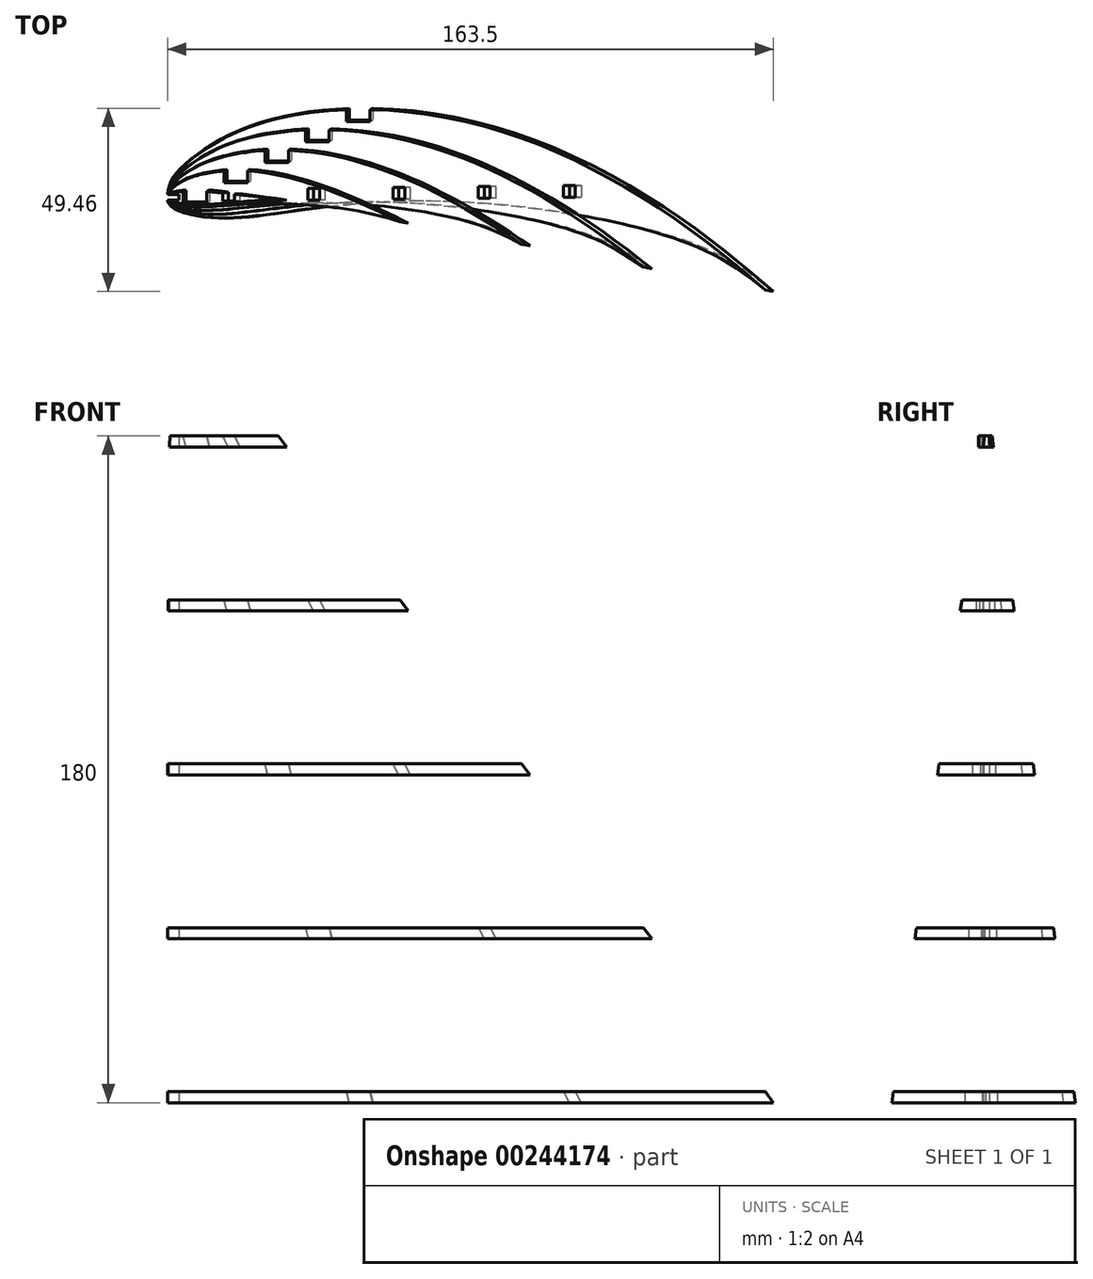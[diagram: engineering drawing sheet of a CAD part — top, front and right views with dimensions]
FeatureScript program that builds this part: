
annotation { "Feature Type Name" : "Feature", "Feature Type Description" : "" }
export const myFeature = defineFeature(function(context is Context, id is Id, definition is map)
    precondition{}
    {
        {
            var Q0;
            Q0=qCreatedBy(makeId("Top.planeOp"),FACE);
            var sketch = newSketch(context, id + "F0", { "sketchPlane" : qUnion([Q0])});
            skLineSegment(sketch, "E0", {"start": v(1.56, 5.68) * mm, "end": v(5.56, 9.57) * mm});
            skLineSegment(sketch, "E1", {"start": v(5.56, 9.57) * mm, "end": v(7.64, 11.4) * mm});
            skLineSegment(sketch, "E2", {"start": v(7.64, 11.4) * mm, "end": v(10.4, 13.54) * mm});
            skLineSegment(sketch, "E3", {"start": v(10.4, 13.54) * mm, "end": v(12.1, 14.65) * mm});
            skLineSegment(sketch, "E4", {"start": v(12.1, 14.65) * mm, "end": v(14.51, 16.01) * mm});
            skLineSegment(sketch, "E5", {"start": v(14.51, 16.01) * mm, "end": v(17.02, 17.22) * mm});
            skLineSegment(sketch, "E6", {"start": v(17.02, 17.22) * mm, "end": v(19.6, 18.28) * mm});
            skLineSegment(sketch, "E7", {"start": v(19.6, 18.28) * mm, "end": v(22.25, 19.22) * mm});
            skLineSegment(sketch, "E8", {"start": v(22.25, 19.22) * mm, "end": v(25.63, 20.25) * mm});
            skLineSegment(sketch, "E9", {"start": v(25.63, 20.25) * mm, "end": v(27.63, 20.8) * mm});
            skLineSegment(sketch, "E10", {"start": v(27.63, 20.8) * mm, "end": v(30.34, 21.45) * mm});
            skLineSegment(sketch, "E11", {"start": v(30.34, 21.45) * mm, "end": v(33.06, 22.02) * mm});
            skLineSegment(sketch, "E12", {"start": v(33.06, 22.02) * mm, "end": v(35.8, 22.52) * mm});
            skLineSegment(sketch, "E13", {"start": v(35.8, 22.52) * mm, "end": v(38.53, 22.94) * mm});
            skLineSegment(sketch, "E14", {"start": v(38.53, 22.94) * mm, "end": v(41.28, 23.3) * mm});
            skLineSegment(sketch, "E15", {"start": v(41.28, 23.3) * mm, "end": v(45.44, 23.69) * mm});
            skLineSegment(sketch, "E16", {"start": v(45.44, 23.69) * mm, "end": v(52.36, 24.01) * mm});
            skLineSegment(sketch, "E17", {"start": v(52.36, 24.01) * mm, "end": v(57.92, 23.98) * mm});
            skLineSegment(sketch, "E18", {"start": v(57.92, 23.98) * mm, "end": v(63.48, 23.67) * mm});
            skLineSegment(sketch, "E19", {"start": v(63.48, 23.67) * mm, "end": v(68.2, 23.2) * mm});
            skLineSegment(sketch, "E20", {"start": v(68.2, 23.2) * mm, "end": v(74.5, 22.25) * mm});
            skLineSegment(sketch, "E21", {"start": v(74.5, 22.25) * mm, "end": v(79.94, 21.16) * mm});
            skLineSegment(sketch, "E22", {"start": v(79.94, 21.16) * mm, "end": v(85.34, 19.84) * mm});
            skLineSegment(sketch, "E23", {"start": v(85.34, 19.84) * mm, "end": v(91.78, 17.96) * mm});
            skLineSegment(sketch, "E24", {"start": v(91.78, 17.96) * mm, "end": v(95.97, 16.57) * mm});
            skLineSegment(sketch, "E25", {"start": v(95.97, 16.57) * mm, "end": v(101.2, 14.66) * mm});
            skLineSegment(sketch, "E26", {"start": v(101.2, 14.66) * mm, "end": v(106.35, 12.57) * mm});
            skLineSegment(sketch, "E27", {"start": v(106.35, 12.57) * mm, "end": v(111.41, 10.3) * mm});
            skLineSegment(sketch, "E28", {"start": v(111.41, 10.3) * mm, "end": v(114.54, 8.79) * mm});
            skLineSegment(sketch, "E29", {"start": v(114.54, 8.79) * mm, "end": v(121.24, 5.25) * mm});
            skLineSegment(sketch, "E30", {"start": v(121.24, 5.25) * mm, "end": v(126.03, 2.48) * mm});
            skLineSegment(sketch, "E31", {"start": v(126.03, 2.48) * mm, "end": v(130.76, -0.45) * mm});
            skLineSegment(sketch, "E32", {"start": v(130.76, -0.45) * mm, "end": v(134.68, -3) * mm});
            skLineSegment(sketch, "E33", {"start": v(134.68, -3) * mm, "end": v(140.13, -6.74) * mm});
            skLineSegment(sketch, "E34", {"start": v(140.13, -6.74) * mm, "end": v(144.69, -10.02) * mm});
            skLineSegment(sketch, "E35", {"start": v(144.69, -10.02) * mm, "end": v(150.73, -14.63) * mm});
            skLineSegment(sketch, "E36", {"start": v(150.73, -14.63) * mm, "end": v(153.15, -16.57) * mm});
            skLineSegment(sketch, "E37", {"start": v(153.15, -16.57) * mm, "end": v(155.17, -18.23) * mm});
            skLineSegment(sketch, "E38", {"start": v(155.17, -18.23) * mm, "end": v(157.28, -19.98) * mm});
            skLineSegment(sketch, "E39", {"start": v(157.28, -19.98) * mm, "end": v(159.53, -21.87) * mm});
            skLineSegment(sketch, "E40", {"start": v(159.53, -21.87) * mm, "end": v(161.04, -23.14) * mm});
            skLineSegment(sketch, "E41", {"start": v(161.04, -23.14) * mm, "end": v(162.55, -24.41) * mm});
            skLineSegment(sketch, "E42", {"start": v(162.55, -24.41) * mm, "end": v(163.03, -24.83) * mm});
            skLineSegment(sketch, "E43", {"start": v(163.03, -24.83) * mm, "end": v(163.34, -25.1) * mm});
            skLineSegment(sketch, "E44", {"start": v(163.34, -25.1) * mm, "end": v(163.57, -25.34) * mm});
            skLineSegment(sketch, "E45", {"start": v(163.57, -25.34) * mm, "end": v(163.6, -25.41) * mm});
            skLineSegment(sketch, "E46", {"start": v(163.6, -25.41) * mm, "end": v(163.5, -25.38) * mm});
            skLineSegment(sketch, "E47", {"start": v(163.5, -25.38) * mm, "end": v(163.25, -25.24) * mm});
            skLineSegment(sketch, "E48", {"start": v(163.25, -25.24) * mm, "end": v(162.89, -25.02) * mm});
            skLineSegment(sketch, "E49", {"start": v(162.89, -25.02) * mm, "end": v(162.42, -24.7) * mm});
            skLineSegment(sketch, "E50", {"start": v(162.42, -24.7) * mm, "end": v(161.85, -24.33) * mm});
            skLineSegment(sketch, "E51", {"start": v(161.85, -24.33) * mm, "end": v(161.2, -23.89) * mm});
            skLineSegment(sketch, "E52", {"start": v(161.2, -23.89) * mm, "end": v(160.46, -23.39) * mm});
            skLineSegment(sketch, "E53", {"start": v(160.46, -23.39) * mm, "end": v(158.82, -22.27) * mm});
            skLineSegment(sketch, "E54", {"start": v(158.82, -22.27) * mm, "end": v(157.02, -21.04) * mm});
            skLineSegment(sketch, "E55", {"start": v(157.02, -21.04) * mm, "end": v(153.51, -18.72) * mm});
            skLineSegment(sketch, "E56", {"start": v(153.51, -18.72) * mm, "end": v(151.5, -17.45) * mm});
            skLineSegment(sketch, "E57", {"start": v(151.5, -17.45) * mm, "end": v(149.82, -16.42) * mm});
            skLineSegment(sketch, "E58", {"start": v(149.82, -16.42) * mm, "end": v(148.21, -15.5) * mm});
            skLineSegment(sketch, "E59", {"start": v(148.21, -15.5) * mm, "end": v(146.7, -14.65) * mm});
            skLineSegment(sketch, "E60", {"start": v(146.7, -14.65) * mm, "end": v(145.24, -13.9) * mm});
            skLineSegment(sketch, "E61", {"start": v(145.24, -13.9) * mm, "end": v(143.85, -13.2) * mm});
            skLineSegment(sketch, "E62", {"start": v(143.85, -13.2) * mm, "end": v(142.52, -12.6) * mm});
            skLineSegment(sketch, "E63", {"start": v(142.52, -12.6) * mm, "end": v(141.24, -12.04) * mm});
            skLineSegment(sketch, "E64", {"start": v(141.24, -12.04) * mm, "end": v(138.82, -11.11) * mm});
            skLineSegment(sketch, "E65", {"start": v(138.82, -11.11) * mm, "end": v(136.53, -10.36) * mm});
            skLineSegment(sketch, "E66", {"start": v(136.53, -10.36) * mm, "end": v(134.32, -9.76) * mm});
            skLineSegment(sketch, "E67", {"start": v(134.32, -9.76) * mm, "end": v(129.95, -8.78) * mm});
            skLineSegment(sketch, "E68", {"start": v(129.95, -8.78) * mm, "end": v(128.13, -8.4) * mm});
            skLineSegment(sketch, "E69", {"start": v(128.13, -8.4) * mm, "end": v(125.32, -7.82) * mm});
            skLineSegment(sketch, "E70", {"start": v(125.32, -7.82) * mm, "end": v(122.86, -7.3) * mm});
            skLineSegment(sketch, "E71", {"start": v(122.86, -7.3) * mm, "end": v(120.3, -6.74) * mm});
            skLineSegment(sketch, "E72", {"start": v(120.3, -6.74) * mm, "end": v(114.98, -5.62) * mm});
            skLineSegment(sketch, "E73", {"start": v(114.98, -5.62) * mm, "end": v(109.42, -4.5) * mm});
            skLineSegment(sketch, "E74", {"start": v(109.42, -4.5) * mm, "end": v(103.71, -3.46) * mm});
            skLineSegment(sketch, "E75", {"start": v(103.71, -3.46) * mm, "end": v(97.93, -2.53) * mm});
            skLineSegment(sketch, "E76", {"start": v(97.93, -2.53) * mm, "end": v(91.13, -1.7) * mm});
            skLineSegment(sketch, "E77", {"start": v(91.13, -1.7) * mm, "end": v(86.47, -1.3) * mm});
            skLineSegment(sketch, "E78", {"start": v(86.47, -1.3) * mm, "end": v(80.86, -1.04) * mm});
            skLineSegment(sketch, "E79", {"start": v(80.86, -1.04) * mm, "end": v(75.32, -0.97) * mm});
            skLineSegment(sketch, "E80", {"start": v(75.32, -0.97) * mm, "end": v(69.81, -1.08) * mm});
            skLineSegment(sketch, "E81", {"start": v(69.81, -1.08) * mm, "end": v(64.32, -1.32) * mm});
            skLineSegment(sketch, "E82", {"start": v(64.32, -1.32) * mm, "end": v(53.96, -2.02) * mm});
            skLineSegment(sketch, "E83", {"start": v(53.96, -2.02) * mm, "end": v(47.7, -2.53) * mm});
            skLineSegment(sketch, "E84", {"start": v(47.7, -2.53) * mm, "end": v(36.53, -3.57) * mm});
            skLineSegment(sketch, "E85", {"start": v(36.53, -3.57) * mm, "end": v(31.03, -4.15) * mm});
            skLineSegment(sketch, "E86", {"start": v(31.03, -4.15) * mm, "end": v(25.3, -4.8) * mm});
            skLineSegment(sketch, "E87", {"start": v(25.3, -4.8) * mm, "end": v(20.36, -5.36) * mm});
            skLineSegment(sketch, "E88", {"start": v(20.36, -5.36) * mm, "end": v(17.7, -5.56) * mm});
            skLineSegment(sketch, "E89", {"start": v(17.7, -5.56) * mm, "end": v(14.96, -5.63) * mm});
            skLineSegment(sketch, "E90", {"start": v(14.96, -5.63) * mm, "end": v(12.13, -5.52) * mm});
            skLineSegment(sketch, "E91", {"start": v(12.13, -5.52) * mm, "end": v(10.66, -5.39) * mm});
            skLineSegment(sketch, "E92", {"start": v(10.66, -5.39) * mm, "end": v(9.15, -5.2) * mm});
            skLineSegment(sketch, "E93", {"start": v(9.15, -5.2) * mm, "end": v(7.78, -4.97) * mm});
            skLineSegment(sketch, "E94", {"start": v(7.78, -4.97) * mm, "end": v(6.02, -4.6) * mm});
            skLineSegment(sketch, "E95", {"start": v(6.02, -4.6) * mm, "end": v(4.48, -4.16) * mm});
            skLineSegment(sketch, "E96", {"start": v(4.48, -4.16) * mm, "end": v(3.06, -3.62) * mm});
            skLineSegment(sketch, "E97", {"start": v(3.06, -3.62) * mm, "end": v(1.82, -2.95) * mm});
            skLineSegment(sketch, "E98", {"start": v(1.82, -2.95) * mm, "end": v(1.3, -2.56) * mm});
            skLineSegment(sketch, "E99", {"start": v(1.3, -2.56) * mm, "end": v(0.85, -2.13) * mm});
            skLineSegment(sketch, "E100", {"start": v(0.85, -2.13) * mm, "end": v(0.5, -1.66) * mm});
            skLineSegment(sketch, "E101", {"start": v(0.5, -1.66) * mm, "end": v(0.25, -1.2) * mm});
            skLineSegment(sketch, "E102", {"start": v(0.25, -1.2) * mm, "end": v(0.07, -0.6) * mm});
            skLineSegment(sketch, "E103", {"start": v(0.07, -0.6) * mm, "end": v(0, 0) * mm});
            skLineSegment(sketch, "E104", {"start": v(0, 0) * mm, "end": v(0.01, 0.63) * mm});
            skLineSegment(sketch, "E105", {"start": v(0.01, 0.63) * mm, "end": v(0.1, 1.3) * mm});
            skLineSegment(sketch, "E106", {"start": v(0.1, 1.3) * mm, "end": v(0.45, 2.7) * mm});
            skLineSegment(sketch, "E107", {"start": v(0.45, 2.7) * mm, "end": v(0.96, 4.17) * mm});
            skLineSegment(sketch, "E108", {"start": v(0.96, 4.17) * mm, "end": v(1.56, 5.68) * mm});
            skSolve(sketch);
        }
        {
            var Q0;
            Q0=qCreatedBy(makeId("Top.planeOp"),FACE);
            var sketch = newSketch(context, id + "F1", { "sketchPlane" : qUnion([Q0])});
            skPoint(sketch, "E109.0", {"position": v(0, 0) * mm});
            skPoint(sketch, "E109.1", {"position": v(5.56, 9.57) * mm});
            skPoint(sketch, "E109.2", {"position": v(22.25, 19.22) * mm});
            skPoint(sketch, "E109.3", {"position": v(57.92, 23.98) * mm});
            skPoint(sketch, "E109.4", {"position": v(101.2, 14.66) * mm});
            skPoint(sketch, "E109.5", {"position": v(140.13, -6.74) * mm});
            skPoint(sketch, "E109.6", {"position": v(163.6, -25.41) * mm});
            skPoint(sketch, "E109.7", {"position": v(0.25, -1.2) * mm});
            skPoint(sketch, "E109.8", {"position": v(1.82, -2.95) * mm});
            skPoint(sketch, "E109.9", {"position": v(12.13, -5.52) * mm});
            skPoint(sketch, "E109.10", {"position": v(0.96, 4.17) * mm});
            skPoint(sketch, "E109.11", {"position": v(31.03, -4.15) * mm});
            skPoint(sketch, "E109.12", {"position": v(75.32, -0.97) * mm});
            skPoint(sketch, "E109.13", {"position": v(142.52, -12.6) * mm});
            skFitSpline(sketch, "E110", {"points": [v(0, 0) * mm, v(0.96, 4.17) * mm, v(5.56, 9.57) * mm, v(22.25, 19.22) * mm, v(57.92, 23.98) * mm, v(101.2, 14.66) * mm, v(140.13, -6.74) * mm, v(163.6, -25.41) * mm], "startDerivative": vector(8.48, 68.87) * mm, "endDerivative": vector(134, -114.38) * mm});
            skFitSpline(sketch, "E111", {"points": [v(0, 0) * mm, v(0.25, -1.2) * mm, v(1.82, -2.95) * mm, v(12.13, -5.52) * mm, v(31.03, -4.15) * mm, v(75.32, -0.97) * mm, v(142.52, -12.6) * mm, v(163.6, -25.41) * mm], "startDerivative": vector(3.77, -32.14) * mm, "endDerivative": vector(102.14, -81.68) * mm});
            skSolve(sketch);
        }
        {
            var Q0;
            Q0=qCreatedBy(makeId("Top.planeOp"),FACE);
            cPlane(context, id + "F2", {"entities" : qUnion([Q0]), "cplaneType" : CPlaneType.OFFSET, "offset" : 180 * mm, "width" : 150 * mm, "height" : 150 * mm});
        }
        {
            var Q0;
            Q0=qCreatedBy(id+"F2.planeOp",FACE);
            var sketch = newSketch(context, id + "F3", { "sketchPlane" : qUnion([Q0])});
            skLineSegment(sketch, "E112", {"start": v(0, 0) * mm, "end": v(0.3, 0.38) * mm});
            skLineSegment(sketch, "E113", {"start": v(0.3, 0.38) * mm, "end": v(0.47, 0.56) * mm});
            skLineSegment(sketch, "E114", {"start": v(0.47, 0.56) * mm, "end": v(0.63, 0.72) * mm});
            skLineSegment(sketch, "E115", {"start": v(0.63, 0.72) * mm, "end": v(0.8, 0.86) * mm});
            skLineSegment(sketch, "E116", {"start": v(0.8, 0.86) * mm, "end": v(1, 1) * mm});
            skLineSegment(sketch, "E117", {"start": v(1, 1) * mm, "end": v(1.22, 1.1) * mm});
            skLineSegment(sketch, "E118", {"start": v(1.22, 1.1) * mm, "end": v(1.43, 1.2) * mm});
            skLineSegment(sketch, "E119", {"start": v(1.43, 1.2) * mm, "end": v(1.66, 1.26) * mm});
            skLineSegment(sketch, "E120", {"start": v(1.66, 1.26) * mm, "end": v(1.9, 1.32) * mm});
            skLineSegment(sketch, "E121", {"start": v(1.9, 1.32) * mm, "end": v(2.38, 1.4) * mm});
            skLineSegment(sketch, "E122", {"start": v(2.38, 1.4) * mm, "end": v(3.07, 1.49) * mm});
            skLineSegment(sketch, "E123", {"start": v(3.07, 1.49) * mm, "end": v(4.34, 1.61) * mm});
            skLineSegment(sketch, "E124", {"start": v(4.34, 1.61) * mm, "end": v(5.28, 1.69) * mm});
            skLineSegment(sketch, "E125", {"start": v(5.28, 1.69) * mm, "end": v(6.67, 1.76) * mm});
            skLineSegment(sketch, "E126", {"start": v(6.67, 1.76) * mm, "end": v(7.17, 1.76) * mm});
            skLineSegment(sketch, "E127", {"start": v(7.17, 1.76) * mm, "end": v(8.12, 1.75) * mm});
            skLineSegment(sketch, "E128", {"start": v(8.12, 1.75) * mm, "end": v(9.07, 1.72) * mm});
            skLineSegment(sketch, "E129", {"start": v(9.07, 1.72) * mm, "end": v(10.03, 1.66) * mm});
            skLineSegment(sketch, "E130", {"start": v(10.03, 1.66) * mm, "end": v(11.22, 1.58) * mm});
            skLineSegment(sketch, "E131", {"start": v(11.22, 1.58) * mm, "end": v(12.9, 1.43) * mm});
            skLineSegment(sketch, "E132", {"start": v(12.9, 1.43) * mm, "end": v(14.8, 1.24) * mm});
            skLineSegment(sketch, "E133", {"start": v(14.8, 1.24) * mm, "end": v(16.34, 1.07) * mm});
            skLineSegment(sketch, "E134", {"start": v(16.34, 1.07) * mm, "end": v(18.57, 0.8) * mm});
            skLineSegment(sketch, "E135", {"start": v(18.57, 0.8) * mm, "end": v(20.47, 0.56) * mm});
            skLineSegment(sketch, "E136", {"start": v(20.47, 0.56) * mm, "end": v(21.43, 0.45) * mm});
            skLineSegment(sketch, "E137", {"start": v(21.43, 0.45) * mm, "end": v(22.43, 0.33) * mm});
            skLineSegment(sketch, "E138", {"start": v(22.43, 0.33) * mm, "end": v(23.42, 0.21) * mm});
            skLineSegment(sketch, "E139", {"start": v(23.42, 0.21) * mm, "end": v(24.38, 0.1) * mm});
            skLineSegment(sketch, "E140", {"start": v(24.38, 0.1) * mm, "end": v(24.84, 0.04) * mm});
            skLineSegment(sketch, "E141", {"start": v(24.84, 0.04) * mm, "end": v(25.3, -0.01) * mm});
            skLineSegment(sketch, "E142", {"start": v(25.3, -0.01) * mm, "end": v(25.9, -0.09) * mm});
            skLineSegment(sketch, "E143", {"start": v(25.9, -0.09) * mm, "end": v(26.15, -0.12) * mm});
            skLineSegment(sketch, "E144", {"start": v(26.15, -0.12) * mm, "end": v(26.97, -0.22) * mm});
            skLineSegment(sketch, "E145", {"start": v(26.97, -0.22) * mm, "end": v(27.4, -0.27) * mm});
            skLineSegment(sketch, "E146", {"start": v(27.4, -0.27) * mm, "end": v(27.65, -0.29) * mm});
            skLineSegment(sketch, "E147", {"start": v(27.65, -0.29) * mm, "end": v(27.9, -0.3) * mm});
            skLineSegment(sketch, "E148", {"start": v(27.9, -0.3) * mm, "end": v(28.16, -0.32) * mm});
            skLineSegment(sketch, "E149", {"start": v(28.16, -0.32) * mm, "end": v(28.45, -0.34) * mm});
            skLineSegment(sketch, "E150", {"start": v(28.45, -0.34) * mm, "end": v(28.76, -0.35) * mm});
            skLineSegment(sketch, "E151", {"start": v(28.76, -0.35) * mm, "end": v(28.93, -0.36) * mm});
            skLineSegment(sketch, "E152", {"start": v(28.93, -0.36) * mm, "end": v(29.42, -0.37) * mm});
            skLineSegment(sketch, "E153", {"start": v(29.42, -0.37) * mm, "end": v(29.57, -0.37) * mm});
            skLineSegment(sketch, "E154", {"start": v(29.57, -0.37) * mm, "end": v(29.71, -0.38) * mm});
            skLineSegment(sketch, "E155", {"start": v(29.71, -0.38) * mm, "end": v(29.83, -0.38) * mm});
            skLineSegment(sketch, "E156", {"start": v(29.83, -0.38) * mm, "end": v(29.92, -0.38) * mm});
            skLineSegment(sketch, "E157", {"start": v(29.92, -0.38) * mm, "end": v(29.98, -0.38) * mm});
            skLineSegment(sketch, "E158", {"start": v(29.98, -0.38) * mm, "end": v(30, -0.39) * mm});
            skLineSegment(sketch, "E159", {"start": v(30, -0.39) * mm, "end": v(29.98, -0.39) * mm});
            skLineSegment(sketch, "E160", {"start": v(29.98, -0.39) * mm, "end": v(29.92, -0.4) * mm});
            skLineSegment(sketch, "E161", {"start": v(29.92, -0.4) * mm, "end": v(29.83, -0.4) * mm});
            skLineSegment(sketch, "E162", {"start": v(29.83, -0.4) * mm, "end": v(29.72, -0.4) * mm});
            skLineSegment(sketch, "E163", {"start": v(29.72, -0.4) * mm, "end": v(29.58, -0.4) * mm});
            skLineSegment(sketch, "E164", {"start": v(29.58, -0.4) * mm, "end": v(29.42, -0.4) * mm});
            skLineSegment(sketch, "E165", {"start": v(29.42, -0.4) * mm, "end": v(28.93, -0.42) * mm});
            skLineSegment(sketch, "E166", {"start": v(28.93, -0.42) * mm, "end": v(28.76, -0.42) * mm});
            skLineSegment(sketch, "E167", {"start": v(28.76, -0.42) * mm, "end": v(28.45, -0.43) * mm});
            skLineSegment(sketch, "E168", {"start": v(28.45, -0.43) * mm, "end": v(28.17, -0.44) * mm});
            skLineSegment(sketch, "E169", {"start": v(28.17, -0.44) * mm, "end": v(27.9, -0.46) * mm});
            skLineSegment(sketch, "E170", {"start": v(27.9, -0.46) * mm, "end": v(27.65, -0.47) * mm});
            skLineSegment(sketch, "E171", {"start": v(27.65, -0.47) * mm, "end": v(27.4, -0.49) * mm});
            skLineSegment(sketch, "E172", {"start": v(27.4, -0.49) * mm, "end": v(26.96, -0.52) * mm});
            skLineSegment(sketch, "E173", {"start": v(26.96, -0.52) * mm, "end": v(26.14, -0.6) * mm});
            skLineSegment(sketch, "E174", {"start": v(26.14, -0.6) * mm, "end": v(25.86, -0.62) * mm});
            skLineSegment(sketch, "E175", {"start": v(25.86, -0.62) * mm, "end": v(25.3, -0.68) * mm});
            skLineSegment(sketch, "E176", {"start": v(25.3, -0.68) * mm, "end": v(24.84, -0.72) * mm});
            skLineSegment(sketch, "E177", {"start": v(24.84, -0.72) * mm, "end": v(24.37, -0.77) * mm});
            skLineSegment(sketch, "E178", {"start": v(24.37, -0.77) * mm, "end": v(23.4, -0.86) * mm});
            skLineSegment(sketch, "E179", {"start": v(23.4, -0.86) * mm, "end": v(22.42, -0.95) * mm});
            skLineSegment(sketch, "E180", {"start": v(22.42, -0.95) * mm, "end": v(21.43, -1.04) * mm});
            skLineSegment(sketch, "E181", {"start": v(21.43, -1.04) * mm, "end": v(20.45, -1.13) * mm});
            skLineSegment(sketch, "E182", {"start": v(20.45, -1.13) * mm, "end": v(18.55, -1.3) * mm});
            skLineSegment(sketch, "E183", {"start": v(18.55, -1.3) * mm, "end": v(16.28, -1.52) * mm});
            skLineSegment(sketch, "E184", {"start": v(16.28, -1.52) * mm, "end": v(12.87, -1.8) * mm});
            skLineSegment(sketch, "E185", {"start": v(12.87, -1.8) * mm, "end": v(11.19, -1.9) * mm});
            skLineSegment(sketch, "E186", {"start": v(11.19, -1.9) * mm, "end": v(10, -1.95) * mm});
            skLineSegment(sketch, "E187", {"start": v(10, -1.95) * mm, "end": v(9.03, -1.98) * mm});
            skLineSegment(sketch, "E188", {"start": v(9.03, -1.98) * mm, "end": v(8.08, -1.98) * mm});
            skLineSegment(sketch, "E189", {"start": v(8.08, -1.98) * mm, "end": v(7.13, -1.96) * mm});
            skLineSegment(sketch, "E190", {"start": v(7.13, -1.96) * mm, "end": v(6.6, -1.93) * mm});
            skLineSegment(sketch, "E191", {"start": v(6.6, -1.93) * mm, "end": v(5.24, -1.83) * mm});
            skLineSegment(sketch, "E192", {"start": v(5.24, -1.83) * mm, "end": v(4.3, -1.74) * mm});
            skLineSegment(sketch, "E193", {"start": v(4.3, -1.74) * mm, "end": v(3.04, -1.58) * mm});
            skLineSegment(sketch, "E194", {"start": v(3.04, -1.58) * mm, "end": v(2.35, -1.47) * mm});
            skLineSegment(sketch, "E195", {"start": v(2.35, -1.47) * mm, "end": v(1.87, -1.37) * mm});
            skLineSegment(sketch, "E196", {"start": v(1.87, -1.37) * mm, "end": v(1.64, -1.3) * mm});
            skLineSegment(sketch, "E197", {"start": v(1.64, -1.3) * mm, "end": v(1.41, -1.22) * mm});
            skLineSegment(sketch, "E198", {"start": v(1.41, -1.22) * mm, "end": v(1.2, -1.13) * mm});
            skLineSegment(sketch, "E199", {"start": v(1.2, -1.13) * mm, "end": v(1, -1.01) * mm});
            skLineSegment(sketch, "E200", {"start": v(1, -1.01) * mm, "end": v(0.77, -0.86) * mm});
            skLineSegment(sketch, "E201", {"start": v(0.77, -0.86) * mm, "end": v(0.62, -0.73) * mm});
            skLineSegment(sketch, "E202", {"start": v(0.62, -0.73) * mm, "end": v(0.46, -0.57) * mm});
            skLineSegment(sketch, "E203", {"start": v(0.46, -0.57) * mm, "end": v(0.3, -0.38) * mm});
            skLineSegment(sketch, "E204", {"start": v(0.3, -0.38) * mm, "end": v(0, 0) * mm});
            skSolve(sketch);
        }
        {
            var Q0;
            Q0=qCreatedBy(id+"F2.planeOp",FACE);
            var sketch = newSketch(context, id + "F4", { "sketchPlane" : qUnion([Q0])});
            skPoint(sketch, "E205.0", {"position": v(0, 0) * mm});
            skPoint(sketch, "E205.1", {"position": v(0.47, 0.56) * mm});
            skPoint(sketch, "E205.2", {"position": v(1, 1) * mm});
            skPoint(sketch, "E205.3", {"position": v(1.9, 1.32) * mm});
            skPoint(sketch, "E205.4", {"position": v(6.67, 1.76) * mm});
            skPoint(sketch, "E205.5", {"position": v(10.03, 1.66) * mm});
            skPoint(sketch, "E205.6", {"position": v(18.57, 0.8) * mm});
            skPoint(sketch, "E205.7", {"position": v(30, -0.39) * mm});
            skPoint(sketch, "E205.8", {"position": v(0.46, -0.57) * mm});
            skPoint(sketch, "E205.9", {"position": v(1, -1.01) * mm});
            skPoint(sketch, "E205.10", {"position": v(1.87, -1.37) * mm});
            skPoint(sketch, "E205.11", {"position": v(6.6, -1.93) * mm});
            skPoint(sketch, "E205.12", {"position": v(10, -1.95) * mm});
            skPoint(sketch, "E205.13", {"position": v(18.55, -1.3) * mm});
            skFitSpline(sketch, "E206", {"points": [v(0, 0) * mm, v(0.47, 0.56) * mm, v(1, 1) * mm, v(1.9, 1.32) * mm, v(6.67, 1.76) * mm, v(10.03, 1.66) * mm, v(18.57, 0.8) * mm, v(30, -0.39) * mm], "startDerivative": vector(6.75, 8.84) * mm, "endDerivative": vector(44, -4.53) * mm});
            skFitSpline(sketch, "E207", {"points": [v(0, 0) * mm, v(0.46, -0.57) * mm, v(1, -1.01) * mm, v(1.87, -1.37) * mm, v(6.6, -1.93) * mm, v(10, -1.95) * mm, v(18.55, -1.3) * mm, v(30, -0.39) * mm], "startDerivative": vector(6.61, -8.92) * mm, "endDerivative": vector(44.1, 3.52) * mm});
            skSolve(sketch);
        }
        {
            var Q0;
            Q0=qCreatedBy(makeId("Front.planeOp"),FACE);
            var sketch = newSketch(context, id + "F5", { "sketchPlane" : qUnion([Q0])});
            skLineSegment(sketch, "E208", {"start": v(0, 0) * mm, "end": v(0, 180) * mm});
            skSolve(sketch);
        }
        {
            var Q0;
            Q0=makeQuery(id+"F1.imprint","IMPRINT",FACE,{"disambiguationData":[TD([[makeQuery(id+"F1.imprint","IMPRINT",EDGE,{"derivedFrom":sQuery(id+"F1.wireOp",EDGE,"E110")}),-1.0]])]});
            var Q1;
            Q1=makeQuery(id+"F4.imprint","IMPRINT",FACE,{"disambiguationData":[TD([[makeQuery(id+"F4.imprint","IMPRINT",EDGE,{"derivedFrom":sQuery(id+"F4.wireOp",EDGE,"E206")}),-1.0]])]});
            var Q2;
            Q2=sQuery(id+"F5.wireOp",EDGE,"E208");
            loft(context, id + "F6", {"addGuides" : true, "sheetProfilesArray" : [{ "sheetProfileEntities" : qUnion([Q0]) }, { "sheetProfileEntities" : qUnion([Q1]) }], "guidesArray" : [{ "guideEntities" : qUnion([Q2]), "guideDerivativeType" : LoftGuideDerivativeType.DEFAULT, "guideDerivativeMagnitude" : 1 }]});
        }
        {
            var Q0;
            Q0=qCreatedBy(makeId("Front.planeOp"),FACE);
            var sketch = newSketch(context, id + "F7", { "sketchPlane" : qUnion([Q0])});
            skLineSegment(sketch, "E209", {"start": v(0, 0) * mm, "end": v(0, 3) * mm, "construction": true});
            skLineSegment(sketch, "E210.bottom", {"start": v(0, 3) * mm, "end": v(200, 3) * mm});
            skLineSegment(sketch, "E210.top", {"start": v(0, 44.25) * mm, "end": v(200, 44.25) * mm});
            skLineSegment(sketch, "E210.left", {"start": v(0, 3) * mm, "end": v(0, 44.25) * mm});
            skLineSegment(sketch, "E210.right", {"start": v(200, 3) * mm, "end": v(200, 44.25) * mm});
            skLineSegment(sketch, "E211.0.1.0", {"start": v(200, 47.25) * mm, "end": v(200, 88.5) * mm});
            skLineSegment(sketch, "E211.0.1.1", {"start": v(0, 47.25) * mm, "end": v(0, 88.5) * mm});
            skLineSegment(sketch, "E211.0.1.2", {"start": v(0, 88.5) * mm, "end": v(200, 88.5) * mm});
            skLineSegment(sketch, "E211.0.1.3", {"start": v(0, 47.25) * mm, "end": v(200, 47.25) * mm});
            skLineSegment(sketch, "E211.0.1.4", {"start": v(0, 44.25) * mm, "end": v(0, 47.25) * mm, "construction": true});
            skLineSegment(sketch, "E211.0.2.0", {"start": v(200, 91.5) * mm, "end": v(200, 132.75) * mm});
            skLineSegment(sketch, "E211.0.2.1", {"start": v(0, 91.5) * mm, "end": v(0, 132.75) * mm});
            skLineSegment(sketch, "E211.0.2.2", {"start": v(0, 132.75) * mm, "end": v(200, 132.75) * mm});
            skLineSegment(sketch, "E211.0.2.3", {"start": v(0, 91.5) * mm, "end": v(200, 91.5) * mm});
            skLineSegment(sketch, "E211.0.2.4", {"start": v(0, 88.5) * mm, "end": v(0, 91.5) * mm, "construction": true});
            skLineSegment(sketch, "E211.0.3.0", {"start": v(200, 135.75) * mm, "end": v(200, 177) * mm});
            skLineSegment(sketch, "E211.0.3.1", {"start": v(0, 135.75) * mm, "end": v(0, 177) * mm});
            skLineSegment(sketch, "E211.0.3.2", {"start": v(0, 177) * mm, "end": v(200, 177) * mm});
            skLineSegment(sketch, "E211.0.3.3", {"start": v(0, 135.75) * mm, "end": v(200, 135.75) * mm});
            skLineSegment(sketch, "E211.0.3.4", {"start": v(0, 132.75) * mm, "end": v(0, 135.75) * mm, "construction": true});
            skLineSegment(sketch, "E211.direction1", {"start": v(0, 0) * mm, "end": v(25, 0) * mm, "construction": true});
            skLineSegment(sketch, "E211.direction2", {"start": v(0, 0) * mm, "end": v(0, 44.25) * mm, "construction": true});
            skSolve(sketch);
        }
        {
            var Q0;
            Q0 = qSketchRegion(id + "F7", true);
            extrude(context, id + "F8", {"entities" : qUnion([Q0]), "operationType" : NewBodyOperationType.REMOVE, "oppositeDirection" : true, "depth" : 100 * mm, "offsetDistance" : 25 * mm, "hasSecondDirection" : true, "secondDirectionOppositeDirection" : false, "secondDirectionDepth" : 100 * mm});
        }
        {
            var Q0;
            Q0=qCreatedBy(makeId("Top.planeOp"),FACE);
            var sketch = newSketch(context, id + "F9", { "sketchPlane" : qUnion([Q0])});
            skLineSegment(sketch, "E212", {"start": v(0, 0) * mm, "end": v(0, 0.8) * mm});
            skLineSegment(sketch, "E213", {"start": v(0, 0.8) * mm, "end": v(3.18, 0.8) * mm});
            skLineSegment(sketch, "E214", {"start": v(3.18, 0.8) * mm, "end": v(3.18, -0.8) * mm});
            skLineSegment(sketch, "E215", {"start": v(3.18, -0.8) * mm, "end": v(0, -0.8) * mm});
            skLineSegment(sketch, "E216", {"start": v(0, -0.8) * mm, "end": v(0, 0) * mm});
            skSolve(sketch);
        }
        {
            var Q0;
            Q0 = qSketchRegion(id + "F9", true);
            extrude(context, id + "F10", {"entities" : qUnion([Q0]), "operationType" : NewBodyOperationType.REMOVE, "depth" : 200 * mm, "offsetDistance" : 25 * mm});
        }
        {
            var Q0;
            Q0=qCreatedBy(makeId("Top.planeOp"),FACE);
            var sketch = newSketch(context, id + "F11", { "sketchPlane" : qUnion([Q0])});
            skFitSpline(sketch, "E217.0", {"points": [v(163.6, -25.41) * mm, v(160.84, -23.06) * mm, v(156.7, -19.52) * mm, v(150.88, -14.78) * mm, v(146.27, -11.2) * mm, v(141.37, -7.57) * mm, v(136.07, -3.9) * mm, v(130.4, -0.24) * mm, v(124.43, 3.36) * mm, v(118.2, 6.82) * mm, v(111.75, 10.09) * mm, v(105.15, 13.1) * mm, v(98.45, 15.78) * mm, v(91.69, 18.09) * mm, v(82.6, 20.68) * mm, v(71.18, 23) * mm, v(57.48, 24.25) * mm, v(46.22, 24.01) * mm, v(37.63, 23.05) * mm, v(31.5, 21.95) * mm, v(26.7, 20.72) * mm, v(23.1, 19.55) * mm, v(19.67, 18.24) * mm, v(15.71, 16.4) * mm, v(11.55, 14.02) * mm, v(8.58, 11.98) * mm, v(6.53, 10.39) * mm, v(4.7, 8.85) * mm, v(3.2, 7.42) * mm, v(2.06, 6.03) * mm, v(1.36, 5) * mm, v(0.84, 3.96) * mm, v(0.37, 2.56) * mm, v(0.2, 1.5) * mm, v(0.1, 0.8) * mm], "construction": true});
            skLineSegment(sketch, "E218", {"start": v(55.51, 24.05) * mm, "end": v(55.51, 20.87) * mm});
            skLineSegment(sketch, "E219", {"start": v(55.51, 20.87) * mm, "end": v(49.16, 20.87) * mm});
            skLineSegment(sketch, "E220", {"start": v(49.16, 20.87) * mm, "end": v(49.16, 24) * mm});
            skLineSegment(sketch, "E221", {"start": v(49.16, 24) * mm, "end": v(55.51, 24.05) * mm, "construction": true});
            skLineSegment(sketch, "E222", {"start": v(49.16, 24) * mm, "end": v(49.15, 25.12) * mm});
            skLineSegment(sketch, "E223", {"start": v(49.15, 25.12) * mm, "end": v(55.51, 25.17) * mm});
            skLineSegment(sketch, "E224", {"start": v(55.51, 25.17) * mm, "end": v(55.51, 24.05) * mm});
            skSolve(sketch);
        }
        {
            var Q0;
            Q0=makeQuery(id+"F6.opLoft","CAP_FACE",FACE,{"disambiguationData":[OSD([makeQuery(id+"F4.imprint","IMPRINT",FACE,{"disambiguationData":[TD([[makeQuery(id+"F4.imprint","IMPRINT",EDGE,{"derivedFrom":sQuery(id+"F4.wireOp",EDGE,"E206")}),-1.0]])]})])],"isStart":true});
            var sketch = newSketch(context, id + "F12", { "sketchPlane" : qUnion([Q0])});
            skLineSegment(sketch, "E225", {"start": v(7.5, 1.78) * mm, "end": v(7.5, -1.98) * mm, "construction": true});
            skLineSegment(sketch, "E226", {"start": v(0, 0) * mm, "end": v(7.5, 0) * mm, "construction": true});
            skLineSegment(sketch, "E227", {"start": v(7.5, 0) * mm, "end": v(7.5, 1.59) * mm, "construction": true});
            skLineSegment(sketch, "E228", {"start": v(7.5, 1.59) * mm, "end": v(10.68, 1.59) * mm, "construction": true});
            skLineSegment(sketch, "E229", {"start": v(10.68, 1.59) * mm, "end": v(10.68, -1.59) * mm});
            skLineSegment(sketch, "E230", {"start": v(10.68, -1.59) * mm, "end": v(4.33, -1.59) * mm});
            skLineSegment(sketch, "E231", {"start": v(4.33, -1.59) * mm, "end": v(4.33, 0) * mm});
            skLineSegment(sketch, "E232", {"start": v(4.33, 0) * mm, "end": v(4.33, 1.59) * mm});
            skLineSegment(sketch, "E233", {"start": v(4.33, 1.59) * mm, "end": v(7.5, 1.59) * mm, "construction": true});
            skLineSegment(sketch, "E234", {"start": v(4.33, 1.59) * mm, "end": v(4.33, 3.34) * mm});
            skLineSegment(sketch, "E235", {"start": v(4.33, 3.34) * mm, "end": v(10.68, 3.34) * mm});
            skLineSegment(sketch, "E236", {"start": v(10.68, 3.34) * mm, "end": v(10.68, 1.59) * mm});
            skSolve(sketch);
        }
        {
            var Q0;
            Q0=sQuery(id+"F11.wireOp",VERTEX,"E223.start");
            var Q1;
            Q1=sQuery(id+"F11.wireOp",VERTEX,"E220.start");
            var Q2;
            Q2=sQuery(id+"F12.wireOp",VERTEX,"E230.end");
            cPlane(context, id + "F13", {"entities" : qUnion([Q0, Q1, Q2]), "cplaneType" : CPlaneType.THREE_POINT, "offset" : 25 * mm, "width" : 150 * mm, "height" : 150 * mm});
        }
        {
            var Q0;
            Q0=qCreatedBy(id+"F13.planeOp",FACE);
            var sketch = newSketch(context, id + "F14", { "sketchPlane" : qUnion([Q0])});
            skPoint(sketch, "E237.0", {"position": v(20.78, -11.9) * mm});
            skPoint(sketch, "E237.1", {"position": v(-1.68, 173.6) * mm});
            skLineSegment(sketch, "E238", {"start": v(20.78, -11.9) * mm, "end": v(-1.68, 173.6) * mm});
            skSolve(sketch);
        }
        {
            var Q0;
            Q0 = qSketchRegion(id + "F11", true);
            var Q1;
            Q1=sQuery(id+"F14.wireOp",EDGE,"E238");
            sweep(context, id + "F15", {"operationType" : NewBodyOperationType.REMOVE, "profiles" : qUnion([Q0]), "path" : qUnion([Q1])});
        }
        {
            var Q0;
            Q0=qCreatedBy(makeId("Top.planeOp"),FACE);
            var sketch = newSketch(context, id + "F16", { "sketchPlane" : qUnion([Q0])});
            skLineSegment(sketch, "E239.bottom", {"start": v(108.54, 3.18) * mm, "end": v(111.71, 3.18) * mm});
            skLineSegment(sketch, "E239.top", {"start": v(108.54, 0) * mm, "end": v(111.71, 0) * mm});
            skLineSegment(sketch, "E239.left", {"start": v(108.54, 3.18) * mm, "end": v(108.54, 0) * mm});
            skLineSegment(sketch, "E239.right", {"start": v(111.71, 3.18) * mm, "end": v(111.71, 0) * mm});
            skSolve(sketch);
        }
        {
            var Q0;
            {var subQ10=sQuery(id+"F12.wireOp",EDGE,"E229");Q0=makeQuery(id+"F12.imprint","IMPRINT",FACE,{"disambiguationData":[TD([[makeQuery(id+"F12.imprint","IMPRINT",EDGE,{"derivedFrom":subQ10}),1.0]])]});}
            var sketch = newSketch(context, id + "F17", { "sketchPlane" : qUnion([Q0])});
            skLineSegment(sketch, "E240.bottom", {"start": v(14.97, 2.17) * mm, "end": v(18.14, 2.17) * mm});
            skLineSegment(sketch, "E240.top", {"start": v(14.97, -1) * mm, "end": v(18.14, -1) * mm});
            skLineSegment(sketch, "E240.left", {"start": v(14.97, 2.17) * mm, "end": v(14.97, -1) * mm});
            skLineSegment(sketch, "E240.right", {"start": v(18.14, 2.17) * mm, "end": v(18.14, -1) * mm});
            skSolve(sketch);
        }
        {
            var Q0;
            Q0 = qSketchRegion(id + "F16", true);
            var Q1;
            Q1 = qSketchRegion(id + "F17", true);
            var Q2;
            Q2=sQuery(id+"F17.wireOp",VERTEX,"E240.left.end");
            var Q3;
            Q3=sQuery(id+"F16.wireOp",VERTEX,"E239.left.end");
            loft(context, id + "F18", {"operationType" : NewBodyOperationType.REMOVE, "sheetProfilesArray" : [{ "sheetProfileEntities" : qUnion([Q0]) }, { "sheetProfileEntities" : qUnion([Q1]) }], "matchConnections" : true, "connections" : [{ "connectionEntities" : qUnion([Q2, Q3]), "connectionEdgeQueries" : qUnion([]), "connectionEdgeParameters" : [] }]});
        }
    });
